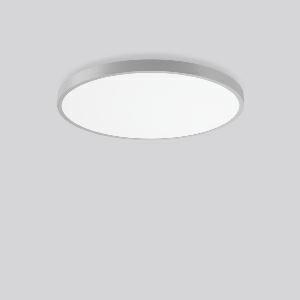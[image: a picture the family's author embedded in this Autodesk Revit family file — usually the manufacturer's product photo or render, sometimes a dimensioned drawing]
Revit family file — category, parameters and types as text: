
# Revit family: triona_round_a_312387_004_1_76_aacf
name_source: partatom
category: Lighting Fixtures
units: mm (PartAtom-declared; Revit-internal decimal feet)

## family parameters
Cut with Voids When Loaded = No
Host = Face
Light Source = No
Part Type = Normal
Room Calculation Point = No
Round Connector Dimension = Use Diameter
Shared = No

## types (1)
- TRIONA round A (1 x LED Modul 840, 8300 lm, 4000)
    Apparent Load = 80 VA
    CIE Flux Codes = 49 80 96 100 100
    Color Rendering = 80
    Color Temperature = 4000
    Default Elevation = 1800 mm
    Description = Series: TRIONA round
Decorative round LED surface-mounted luminaire. Flat, seamless frame: aluminium extrusion profile, powder coated. Cover made of sheet steel, powder-coated. Light emission through a diffuser: plastic, opal. Lightguide and diffuser made of non-yellowing plastic (PMMA). Lateral light emission (RZB SIDELITE technology) for above-average homogeneous light distribution. Suitable for Ceiling mounting, Wall (surface). Tool-free mounting via bayonet connection. Electronic ballast included. Very easy installation thanks to Plug+Play connection. 
Colour: silver, matt (approx. RAL 9006)
Diameter: 845 mm
Height: 88 mm
Lamp: LED
Socket: without socket
Colour temperature: 4000K
Colour rendering index (CRI): 80
System power: 80 W
Rated luminous flux: 8300 lm
Luminous efficiency: 104 lm/W
Control gear: Converter, dimmable, DALI
Protection class: I
Type of protection: IP 20
    Height = 88 mm
    Lamp = 1 x LED Modul 840
    Lamp Light Flux = 8300 lm
    Lamp count = 1
    Length = 845 mm
    Lifetime = 50000 h
    Luminous efficacy = 104 lm/W
    Manufacturer = RZB
    ModVariant = No
    Model = 312387.004.1.76
    Mounting Place = Ceiling
    Mounting Type = Surface mounted
    Number of Poles = 1
    OnlyDefault = Yes
    Power Factor = 1
    Product Name = TRIONA round A
    Product group = Surface mounted modular luminaires
    ProductGroupID = 306
    Protection Class = Protection class I
    Protection Degree = IP 20
    RLX_Detail_Level = 1
    RLX_Emergency_Light_Flux = 0 lm
    RLX_Emergency_Type = 0
    RLX_Emergency_Type_DB = No
    RlxData = <blob elided: 33049 chars, md5=8e4cc0f6>
    Socket = socket
    Standby Power = 0 W
    System Light Flux = 8300 lm
    System Power = 80 W
    Type Comments = Product without accessories
    Type Image = 312388.004.jpg
    URL = http://relux.com
    VarID = ---
    Voltage = 230 V
    Voltage Range = 220-240 V
    Weight = 0.00 kg
    Width = 0 mm  [stored 0 ft]

note: [stored X ft] marks values corroborated as IEEE doubles in the binary element streams (Revit-internal decimal feet)

## geometry (parser evidence)
native form markers: Blend x4, Sweep x9
no freeform markers — native parametric forms only
